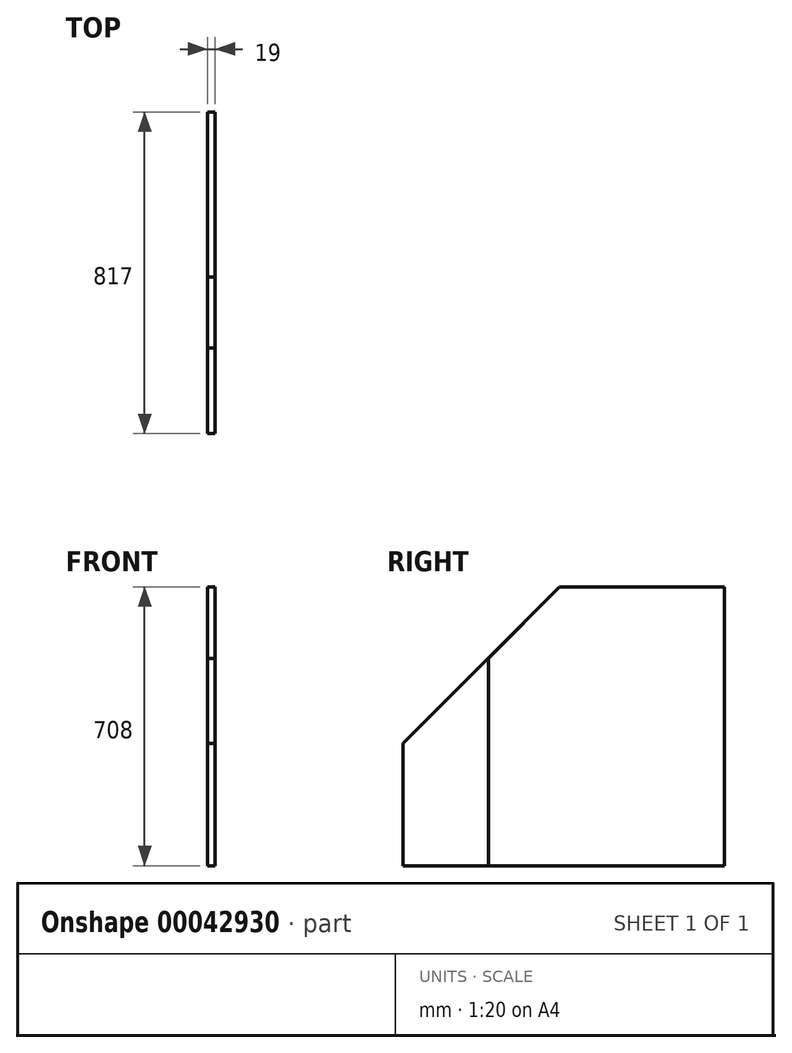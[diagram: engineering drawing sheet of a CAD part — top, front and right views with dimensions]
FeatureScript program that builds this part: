
annotation { "Feature Type Name" : "Feature", "Feature Type Description" : "" }
export const myFeature = defineFeature(function(context is Context, id is Id, definition is map)
    precondition{}
    {
        {
            assignVariable(context, id + "F0", {"name" : "CupboardThickness", "anyValue" : 19});
        }
        {
            var Q0;
            Q0=qCreatedBy(makeId("Right.planeOp"),FACE);
            var sketch = newSketch(context, id + "F1", { "sketchPlane" : qUnion([Q0])});
            skLineSegment(sketch, "E0", {"start": v(0, 0) * mm, "end": v(0, 527) * mm});
            skLineSegment(sketch, "E1", {"start": v(0, 527) * mm, "end": v(181, 708) * mm});
            skLineSegment(sketch, "E2", {"start": v(181, 708) * mm, "end": v(600, 708) * mm});
            skLineSegment(sketch, "E3", {"start": v(600, 708) * mm, "end": v(600, 0) * mm});
            skLineSegment(sketch, "E4", {"start": v(600, 0) * mm, "end": v(0, 0) * mm});
            skLineSegment(sketch, "E5", {"start": v(600, 708) * mm, "end": v(600, 727) * mm, "construction": true});
            skLineSegment(sketch, "E6", {"start": v(600, 727) * mm, "end": v(200, 727) * mm, "construction": true});
            skLineSegment(sketch, "E7", {"start": v(181, 708) * mm, "end": v(200, 727) * mm, "construction": true});
            skSolve(sketch);
        }
        {
            var Q0;
            Q0=makeQuery(id+"F1.imprint","IMPRINT",FACE,{"disambiguationData":[TD([[makeQuery(id+"F1.imprint","IMPRINT",EDGE,{"derivedFrom":sQuery(id+"F1.wireOp",EDGE,"E0")}),-1.0]])]});
            extrude(context, id + "F2", {"entities" : qUnion([Q0]), "depth" : (getVariable(context, 'CupboardThickness')) * mm});
        }
        {
            var Q0;
            Q0=qCreatedBy(makeId("Right.planeOp"),FACE);
            var sketch = newSketch(context, id + "F3", { "sketchPlane" : qUnion([Q0])});
            skLineSegment(sketch, "E8.0", {"start": v(0, 527) * mm, "end": v(181, 708) * mm});
            skLineSegment(sketch, "E9.0", {"start": v(181, 708) * mm, "end": v(600, 708) * mm});
            skLineSegment(sketch, "E10.0", {"start": v(600, 708) * mm, "end": v(600, 0) * mm});
            skLineSegment(sketch, "E11.0", {"start": v(600, 0) * mm, "end": v(0, 0) * mm});
            skLineSegment(sketch, "E12", {"start": v(181, 708) * mm, "end": v(-217, 310) * mm});
            skLineSegment(sketch, "E13", {"start": v(-217, 310) * mm, "end": v(-217, 0) * mm});
            skLineSegment(sketch, "E14", {"start": v(-217, 0) * mm, "end": v(600, 0) * mm});
            skLineSegment(sketch, "E15", {"start": v(600, 708) * mm, "end": v(181, 708) * mm});
            skSolve(sketch);
        }
        {
            var Q0;
            {var subQ1=sQuery(id+"F3.wireOp",EDGE,"E10.0");Q0=makeQuery(id+"F3.imprint","IMPRINT",FACE,{"disambiguationData":[TD([[makeQuery(id+"F3.imprint","IMPRINT",EDGE,{"derivedFrom":subQ1}),-1.0]])]});}
            extrude(context, id + "F4", {"entities" : qUnion([Q0]), "depth" : (getVariable(context, 'CupboardThickness')) * mm});
        }
    });
